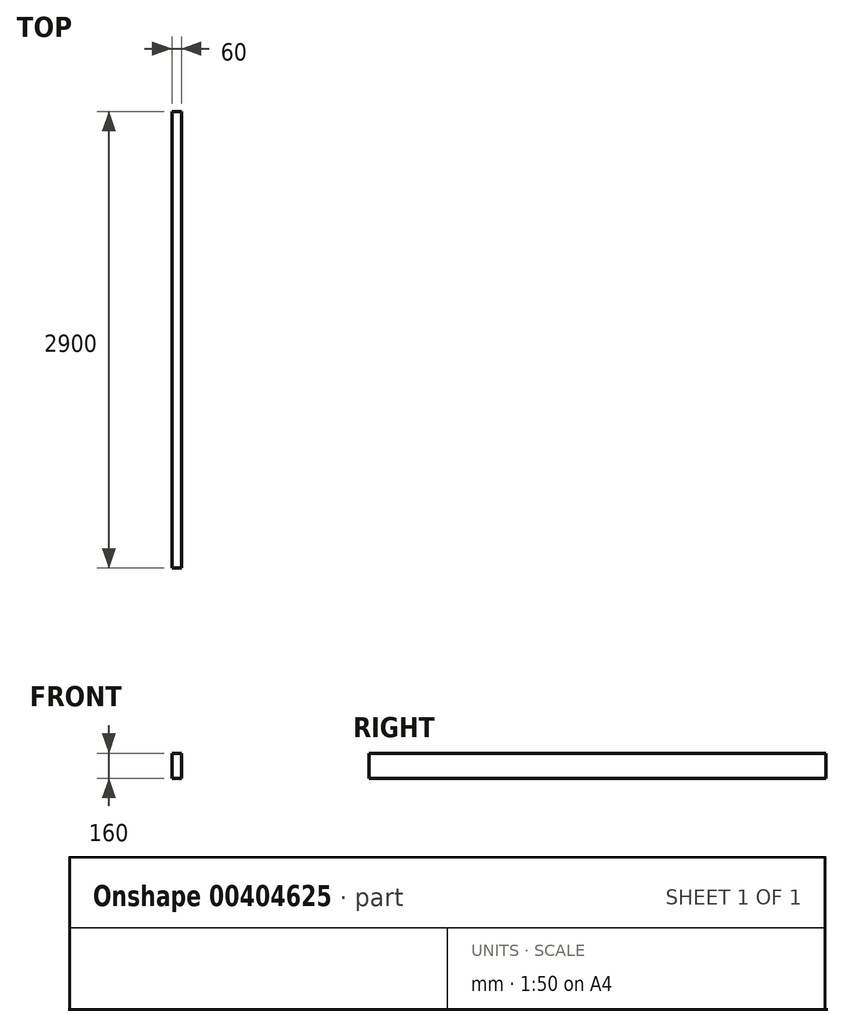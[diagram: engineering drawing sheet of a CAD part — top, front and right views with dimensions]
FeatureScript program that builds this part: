
annotation { "Feature Type Name" : "Feature", "Feature Type Description" : "" }
export const myFeature = defineFeature(function(context is Context, id is Id, definition is map)
    precondition{}
    {
        {
            var Q0;
            Q0=qCreatedBy(makeId("Front.planeOp"),FACE);
            var sketch = newSketch(context, id + "F0", { "sketchPlane" : qUnion([Q0])});
            skLineSegment(sketch, "E0.bottom", {"start": v(-30, 80) * mm, "end": v(30, 80) * mm});
            skLineSegment(sketch, "E0.top", {"start": v(-30, -80) * mm, "end": v(30, -80) * mm});
            skLineSegment(sketch, "E0.left", {"start": v(-30, 80) * mm, "end": v(-30, -80) * mm});
            skLineSegment(sketch, "E0.right", {"start": v(30, 80) * mm, "end": v(30, -80) * mm});
            skSolve(sketch);
        }
        {
            var Q0;
            Q0=qSketchRegion(id+"F0",true);
            extrude(context, id + "F1", {"entities" : qUnion([Q0]), "depth" : 2900 * mm});
        }
    });
